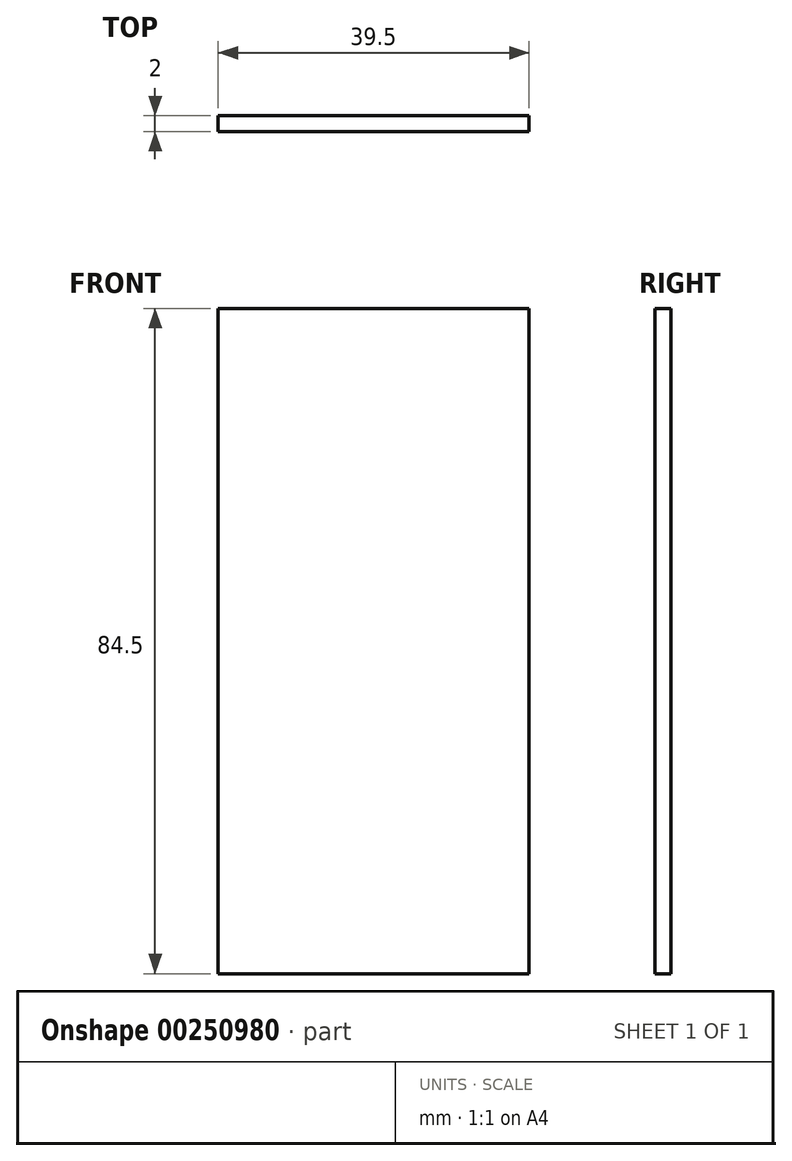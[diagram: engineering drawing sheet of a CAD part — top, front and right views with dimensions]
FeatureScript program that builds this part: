
annotation { "Feature Type Name" : "Feature", "Feature Type Description" : "" }
export const myFeature = defineFeature(function(context is Context, id is Id, definition is map)
    precondition{}
    {
        {
            var Q0;
            Q0=qCreatedBy(makeId("Front.planeOp"),FACE);
            var sketch = newSketch(context, id + "F0", { "sketchPlane" : qUnion([Q0])});
            skLineSegment(sketch, "E0.bottom", {"start": v(-26.85, 26.87) * mm, "end": v(12.65, 26.87) * mm});
            skLineSegment(sketch, "E0.top", {"start": v(-26.85, -57.63) * mm, "end": v(12.65, -57.63) * mm});
            skLineSegment(sketch, "E0.left", {"start": v(-26.85, 26.87) * mm, "end": v(-26.85, -57.63) * mm});
            skLineSegment(sketch, "E0.right", {"start": v(12.65, 26.87) * mm, "end": v(12.65, -57.63) * mm});
            skSolve(sketch);
        }
        {
            var Q0;
            Q0=makeQuery(id+"F0.imprint","IMPRINT",FACE,{"disambiguationData":[TD([[makeQuery(id+"F0.imprint","IMPRINT",EDGE,{"derivedFrom":sQuery(id+"F0.wireOp",EDGE,"E0.bottom")}),-1.0]])]});
            extrude(context, id + "F1", {"entities" : qUnion([Q0]), "depth" : 2 * mm});
        }
    });
